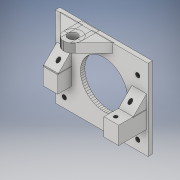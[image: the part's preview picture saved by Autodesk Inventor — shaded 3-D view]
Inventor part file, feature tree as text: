
AUTODESK INVENTOR PART (.ipt)
format: ipt  version: 2017 (Build 210142000, 142)  size: 800,768 bytes
history: native  units: in
note: dims shown in document units (in); Inventor stores cm internally (conversion verified against a paired STEP export)
features: projected_geometry x2, extrude x1, sketch x1, imported_body x1
ambient origin geometry x8: Origin, YZ Plane, XZ Plane, XY Plane, X Axis, Y Axis, Z Axis, Center Point
bodies: Solid1 (feature_tree)
feature tree (5):
  extrude  "Extrusion1"  Depth=0.3937in TaperAngle=0.0deg
  sketch  "Sketch1"  dims[d0=0.252in d1=0.3937in d2=0.0in]
  projected_geometry  "Projected Loop1"
  projected_geometry  "Projected Loop2"
  imported_body  "Base1"
